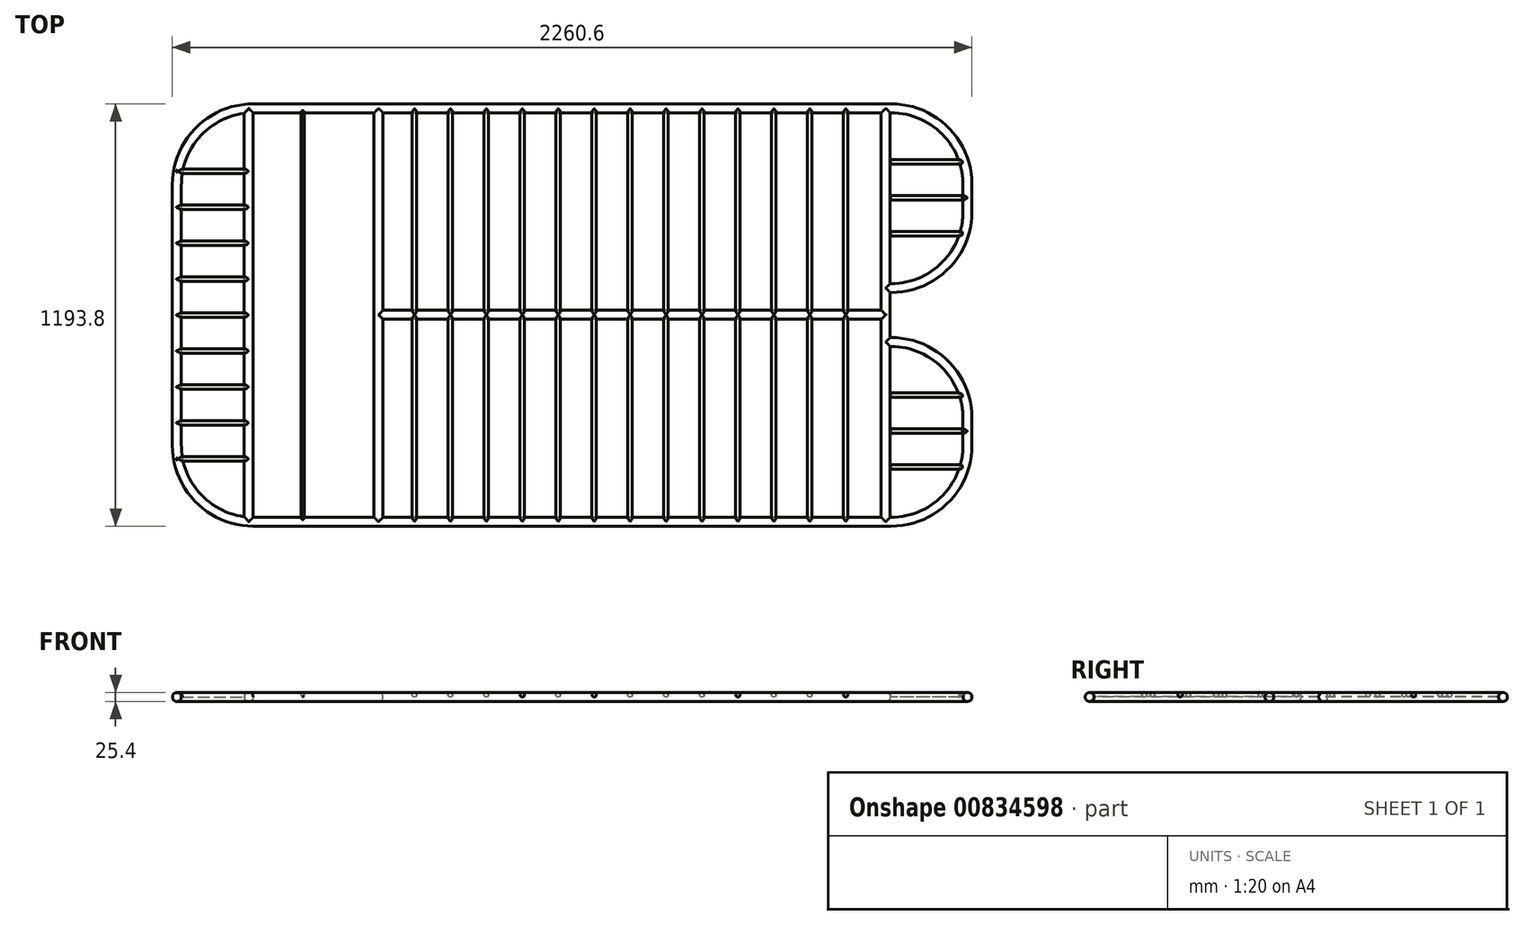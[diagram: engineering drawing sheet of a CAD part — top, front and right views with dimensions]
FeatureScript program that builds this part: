
annotation { "Feature Type Name" : "Feature", "Feature Type Description" : "" }
export const myFeature = defineFeature(function(context is Context, id is Id, definition is map)
    precondition{}
    {
        {
            var Q0;
            Q0=qCreatedBy(makeId("Top.planeOp"),FACE);
            var sketch = newSketch(context, id + "F0", { "sketchPlane" : qUnion([Q0])});
            skLineSegment(sketch, "E0.bottom", {"start": v(215.9, 0) * mm, "end": v(2019.3, 0) * mm});
            skLineSegment(sketch, "E0.top", {"start": v(215.9, 1168.4) * mm, "end": v(2019.3, 1168.4) * mm});
            skLineSegment(sketch, "E0.left", {"start": v(0, 215.9) * mm, "end": v(0, 952.5) * mm});
            skLineSegment(sketch, "E0.right", {"start": v(2235.2, 215.9) * mm, "end": v(2235.2, 292.1) * mm});
            skPoint(sketch, "E1.visualSharp", {"position": v(0, 1168.4) * mm});
            skArc(sketch, "E1.filletArc", {"start": v(215.9, 1168.4) * mm, "mid": v(63.24, 1105.16) * mm, "end": v(0, 952.5) * mm});
            skPoint(sketch, "E2.visualSharp", {"position": v(0, 0) * mm});
            skArc(sketch, "E2.filletArc", {"start": v(0, 215.9) * mm, "mid": v(63.24, 63.24) * mm, "end": v(215.9, 0) * mm});
            skPoint(sketch, "E3.visualSharp", {"position": v(2235.2, 0) * mm});
            skArc(sketch, "E3.filletArc", {"start": v(2019.3, 0) * mm, "mid": v(2171.96, 63.24) * mm, "end": v(2235.2, 215.9) * mm});
            skPoint(sketch, "E4.visualSharp", {"position": v(2235.2, 1168.4) * mm});
            skArc(sketch, "E4.filletArc", {"start": v(2235.2, 952.5) * mm, "mid": v(2171.96, 1105.16) * mm, "end": v(2019.3, 1168.4) * mm});
            skLineSegment(sketch, "E5.bottom", {"start": v(2006.6, 660.4) * mm, "end": v(2019.3, 660.4) * mm});
            skLineSegment(sketch, "E5.top", {"start": v(2006.6, 508) * mm, "end": v(2019.3, 508) * mm});
            skLineSegment(sketch, "E5.left", {"start": v(2006.6, 660.4) * mm, "end": v(2006.6, 508) * mm});
            skLineSegment(sketch, "E6.trimOffspring", {"start": v(2235.2, 876.3) * mm, "end": v(2235.2, 952.5) * mm});
            skPoint(sketch, "E7.visualSharp", {"position": v(2235.2, 660.4) * mm});
            skArc(sketch, "E7.filletArc", {"start": v(2019.3, 660.4) * mm, "mid": v(2171.96, 723.64) * mm, "end": v(2235.2, 876.3) * mm});
            skPoint(sketch, "E8.visualSharp", {"position": v(2235.2, 508) * mm});
            skArc(sketch, "E8.filletArc", {"start": v(2235.2, 292.1) * mm, "mid": v(2171.96, 444.76) * mm, "end": v(2019.3, 508) * mm});
            skSolve(sketch);
        }
        {
            var Q0;
            Q0=qCreatedBy(makeId("Front.planeOp"),FACE);
            cPlane(context, id + "F1", {"entities" : qUnion([Q0]), "cplaneType" : CPlaneType.OFFSET, "offset" : 584.2 * mm, "oppositeDirection" : true, "width" : 152.4 * mm, "height" : 152.4 * mm});
        }
        {
            var Q0;
            Q0=qCreatedBy(id+"F1.planeOp",FACE);
            var sketch = newSketch(context, id + "F2", { "sketchPlane" : qUnion([Q0])});
            skCircle(sketch, "E9", {"center": v(0, 0) * mm, "radius": 12.7 * mm});
            skSolve(sketch);
        }
        {
            var Q0;
            Q0 = qSketchRegion(id + "F2", true);
            var Q1;
            Q1=sQuery(id+"F0.wireOp",EDGE,"E0.left");
            var Q2;
            Q2=sQuery(id+"F0.wireOp",EDGE,"E2.filletArc");
            var Q3;
            Q3=sQuery(id+"F0.wireOp",EDGE,"E0.bottom");
            var Q4;
            Q4=sQuery(id+"F0.wireOp",EDGE,"E1.filletArc");
            var Q5;
            Q5=sQuery(id+"F0.wireOp",EDGE,"E0.top");
            var Q6;
            Q6=sQuery(id+"F0.wireOp",EDGE,"E4.filletArc");
            var Q7;
            Q7=sQuery(id+"F0.wireOp",EDGE,"E6.trimOffspring");
            var Q8;
            Q8=sQuery(id+"F0.wireOp",EDGE,"E7.filletArc");
            var Q9;
            Q9=sQuery(id+"F0.wireOp",EDGE,"E8.filletArc");
            var Q10;
            Q10=sQuery(id+"F0.wireOp",EDGE,"E0.right");
            var Q11;
            Q11=sQuery(id+"F0.wireOp",EDGE,"E3.filletArc");
            sweep(context, id + "F3", {"profiles" : qUnion([Q0]), "path" : qUnion([Q1, Q2, Q3, Q4, Q5, Q6, Q7, Q8, Q9, Q10, Q11])});
        }
        {
            var Q0;
            Q0=qCreatedBy(makeId("Front.planeOp"),FACE);
            var sketch = newSketch(context, id + "F4", { "sketchPlane" : qUnion([Q0])});
            skCircle(sketch, "E10", {"center": v(355.6, 6.35) * mm, "radius": 4.76 * mm});
            skCircle(sketch, "E11", {"center": v(203.2, 0) * mm, "radius": 12.7 * mm});
            skCircle(sketch, "E12", {"center": v(2004.06, 0) * mm, "radius": 12.7 * mm});
            skCircle(sketch, "E13", {"center": v(570.15, 0) * mm, "radius": 12.7 * mm});
            skCircle(sketch, "E14", {"center": v(671.75, 6.35) * mm, "radius": 6.35 * mm});
            skCircle(sketch, "E15", {"center": v(773.35, 6.35) * mm, "radius": 6.35 * mm});
            skCircle(sketch, "E16", {"center": v(874.95, 6.35) * mm, "radius": 6.35 * mm});
            skCircle(sketch, "E17", {"center": v(976.55, 6.35) * mm, "radius": 6.35 * mm});
            skCircle(sketch, "E18", {"center": v(1078.15, 6.35) * mm, "radius": 6.35 * mm});
            skCircle(sketch, "E19", {"center": v(1179.75, 6.35) * mm, "radius": 6.35 * mm});
            skCircle(sketch, "E20", {"center": v(1484.55, 6.35) * mm, "radius": 6.35 * mm});
            skCircle(sketch, "E21", {"center": v(1382.95, 6.35) * mm, "radius": 6.35 * mm});
            skCircle(sketch, "E22", {"center": v(1281.35, 6.35) * mm, "radius": 6.35 * mm});
            skCircle(sketch, "E23", {"center": v(1586.15, 6.35) * mm, "radius": 6.35 * mm});
            skCircle(sketch, "E24", {"center": v(1687.75, 6.35) * mm, "radius": 6.35 * mm});
            skCircle(sketch, "E25", {"center": v(1789.35, 6.35) * mm, "radius": 6.35 * mm});
            skCircle(sketch, "E26", {"center": v(1890.95, 6.35) * mm, "radius": 6.35 * mm});
            skSolve(sketch);
        }
        {
            var Q0;
            Q0 = qSketchRegion(id + "F4", true);
            extrude(context, id + "F5", {"entities" : qUnion([Q0]), "operationType" : NewBodyOperationType.ADD, "oppositeDirection" : true, "depth" : 1168.4 * mm, "offsetDistance" : 25.4 * mm});
        }
        {
            var Q0;
            Q0=qCreatedBy(makeId("Top.planeOp"),FACE);
            var sketch = newSketch(context, id + "F6", { "sketchPlane" : qUnion([Q0])});
            skLineSegment(sketch, "E27", {"start": v(2248.54, 879.48) * mm, "end": v(2248.54, 294.94) * mm, "construction": true});
            skLineSegment(sketch, "E28", {"start": v(419.74, 988.73) * mm, "end": v(419.74, 313.39) * mm, "construction": true});
            skSolve(sketch);
        }
        {
            var Q0;
            Q0=makeQuery(id+"F3.opSweep","CAP_FACE",FACE,{"disambiguationData":[OSD([sQuery(id+"F0.wireOp",VERTEX,"E7.filletArc.start"),sQuery(id+"F2.wireOp",EDGE,"E9")])],"isStart":true});
            var Q1;
            Q1=makeQuery(id+"F3.opSweep","CAP_FACE",FACE,{"disambiguationData":[OSD([sQuery(id+"F0.wireOp",VERTEX,"E8.filletArc.end"),sQuery(id+"F2.wireOp",EDGE,"E9")])],"isStart":false});
            extrude(context, id + "F7", {"entities" : qUnion([Q0, Q1]), "operationType" : NewBodyOperationType.ADD, "endBound" : BoundingType.UP_TO_NEXT, "depth" : 25.4 * mm, "offsetDistance" : 25.4 * mm});
        }
        {
            var Q0;
            Q0=makeQuery(id+"F5.opExtrude","SWEPT_FACE",FACE,{"disambiguationData":[OSD([sQuery(id+"F4.wireOp",EDGE,"E13")])]});
            cPlane(context, id + "F8", {"entities" : qUnion([Q0]), "cplaneType" : CPlaneType.LINE_ANGLE, "offset" : 25.4 * mm, "angle" : 90 * degree, "oppositeDirection" : true, "width" : 152.4 * mm, "height" : 152.4 * mm});
        }
        {
            var Q0;
            Q0=qCreatedBy(id+"F8.planeOp",FACE);
            var sketch = newSketch(context, id + "F9", { "sketchPlane" : qUnion([Q0])});
            skCircle(sketch, "E29", {"center": v(-585, 0) * mm, "radius": 12.7 * mm});
            skSolve(sketch);
        }
        {
            var Q0;
            Q0 = qSketchRegion(id + "F9", true);
            extrude(context, id + "F10", {"entities" : qUnion([Q0]), "operationType" : NewBodyOperationType.ADD, "oppositeDirection" : true, "depth" : 1435.1 * mm, "offsetDistance" : 25.4 * mm});
        }
        {
            var Q0;
            Q0=qCreatedBy(id+"F8.planeOp",FACE);
            var sketch = newSketch(context, id + "F11", { "sketchPlane" : qUnion([Q0])});
            skCircle(sketch, "E30", {"center": v(-584.2, 6.35) * mm, "radius": 6.35 * mm});
            skCircle(sketch, "E31", {"center": v(-482.6, 6.35) * mm, "radius": 6.35 * mm});
            skCircle(sketch, "E32", {"center": v(-381, 6.35) * mm, "radius": 6.35 * mm});
            skCircle(sketch, "E33", {"center": v(-177.8, 6.35) * mm, "radius": 6.35 * mm});
            skCircle(sketch, "E34", {"center": v(-685.8, 6.35) * mm, "radius": 6.35 * mm});
            skCircle(sketch, "E35", {"center": v(-787.4, 6.35) * mm, "radius": 6.35 * mm});
            skCircle(sketch, "E36", {"center": v(-889, 6.35) * mm, "radius": 6.35 * mm});
            skCircle(sketch, "E37", {"center": v(-990.6, 6.35) * mm, "radius": 6.35 * mm});
            skCircle(sketch, "E38", {"center": v(-279.4, 6.35) * mm, "radius": 6.35 * mm});
            skSolve(sketch);
        }
        {
            var Q0;
            Q0 = qSketchRegion(id + "F11", true);
            extrude(context, id + "F12", {"entities" : qUnion([Q0]), "operationType" : NewBodyOperationType.ADD, "depth" : 571.5 * mm, "offsetDistance" : 25.4 * mm, "hasSecondDirection" : true, "secondDirectionOppositeDirection" : false, "secondDirectionDepth" : 368.3 * mm});
        }
        {
            var Q0;
            Q0=qCreatedBy(id+"F8.planeOp",FACE);
            var sketch = newSketch(context, id + "F13", { "sketchPlane" : qUnion([Q0])});
            skCircle(sketch, "E39", {"center": v(-255.9, 6.35) * mm, "radius": 6.35 * mm});
            skCircle(sketch, "E40", {"center": v(-357.5, 6.35) * mm, "radius": 6.35 * mm});
            skCircle(sketch, "E41", {"center": v(-154.3, 6.35) * mm, "radius": 6.35 * mm});
            skCircle(sketch, "E42", {"center": v(-814.07, 6.35) * mm, "radius": 6.35 * mm});
            skCircle(sketch, "E43", {"center": v(-915.67, 6.35) * mm, "radius": 6.35 * mm});
            skCircle(sketch, "E44", {"center": v(-1017.27, 6.35) * mm, "radius": 6.35 * mm});
            skSolve(sketch);
        }
        {
            var Q0;
            Q0 = qSketchRegion(id + "F13", true);
            extrude(context, id + "F14", {"entities" : qUnion([Q0]), "operationType" : NewBodyOperationType.ADD, "oppositeDirection" : true, "depth" : 1651 * mm, "offsetDistance" : 25.4 * mm, "hasSecondDirection" : true, "secondDirectionOppositeDirection" : true, "secondDirectionDepth" : 1447.8 * mm});
        }
        {
            var Q0;
            Q0=makeQuery(id+"F14.opExtrude","CAP_FACE",FACE,{"disambiguationData":[OSD([sQuery(id+"F13.wireOp",EDGE,"E43")])],"isStart":false});
            var Q1;
            Q1=makeQuery(id+"F14.opExtrude","CAP_FACE",FACE,{"disambiguationData":[OSD([sQuery(id+"F13.wireOp",EDGE,"E39")])],"isStart":false});
            var Q2;
            Q2=makeQuery(id+"F3.opSweep","SWEPT_BODY",BODY,{"disambiguationData":[OSD([sQuery(id+"F0.wireOp",EDGE,"E7.filletArc"),sQuery(id+"F2.wireOp",EDGE,"E9")])]});
            extrude(context, id + "F15", {"entities" : qUnion([Q0, Q1]), "endBound" : BoundingType.UP_TO_BODY, "depth" : 25.4 * mm, "endBoundEntityBody" : qUnion([Q2]), "offsetDistance" : 25.4 * mm});
        }
    });
